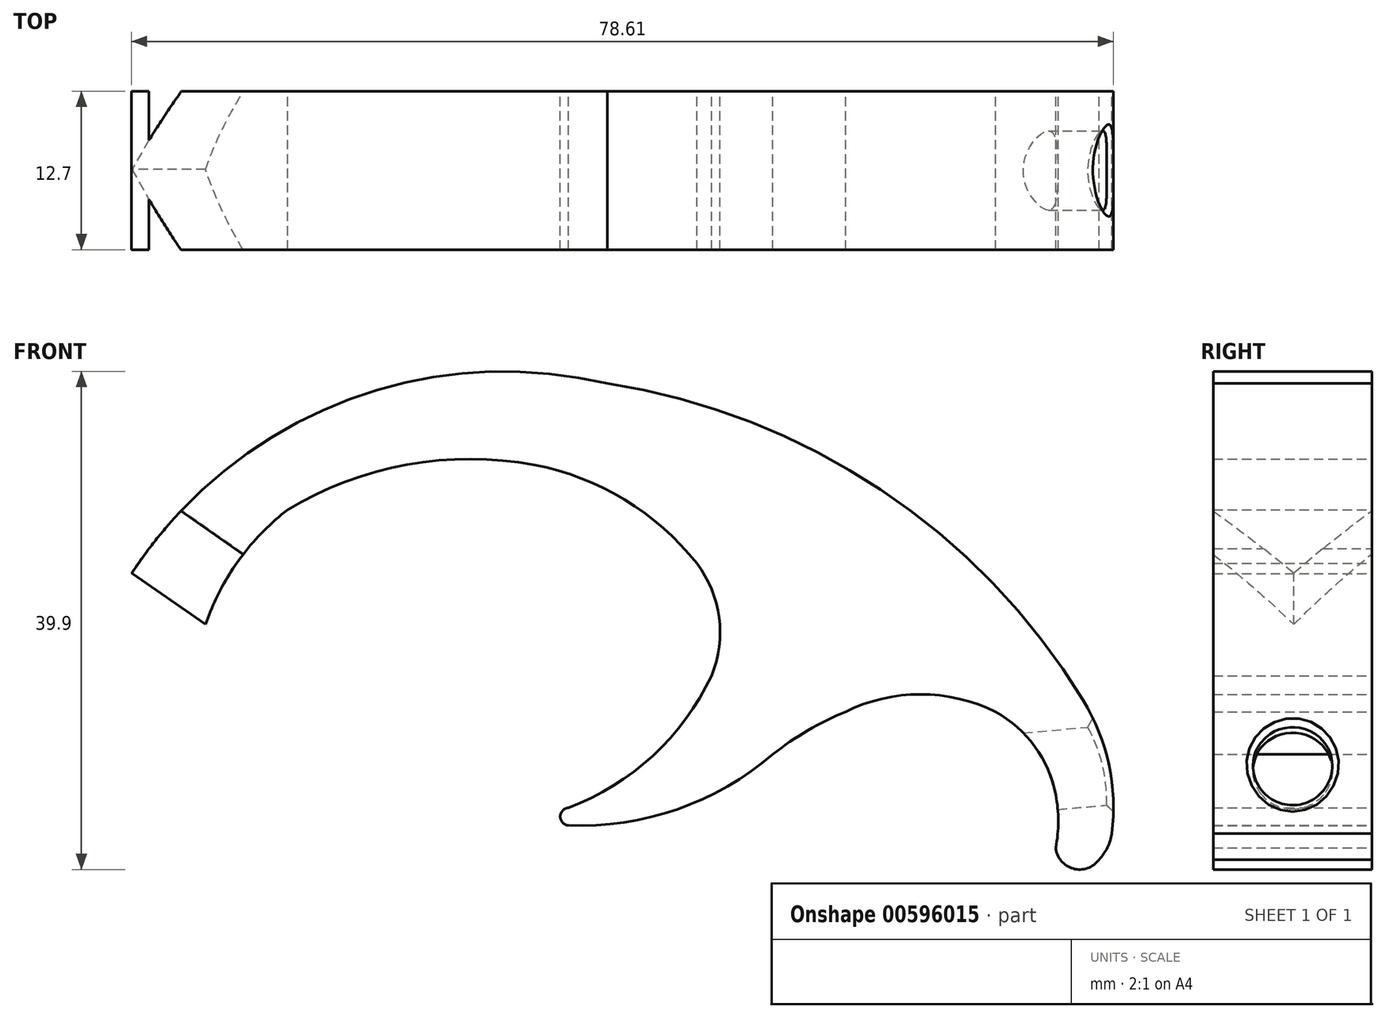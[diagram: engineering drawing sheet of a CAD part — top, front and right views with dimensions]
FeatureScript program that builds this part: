
annotation { "Feature Type Name" : "Feature", "Feature Type Description" : "" }
export const myFeature = defineFeature(function(context is Context, id is Id, definition is map)
    precondition{}
    {
        {
            var Q0;
            Q0=qCreatedBy(makeId("Front.planeOp"),FACE);
            var sketch = newSketch(context, id + "F0", { "sketchPlane" : qUnion([Q0])});
            skLineSegment(sketch, "E0", {"start": v(-79.66, 42.47) * mm, "end": v(-84.59, 51.35) * mm});
            skArc(sketch, "E1", {"start": v(-46.49, 66.6) * mm, "mid": v(-67.95, 65) * mm, "end": v(-84.59, 51.35) * mm});
            skArc(sketch, "E2", {"start": v(-8.39, 41.2) * mm, "mid": v(-24.63, 58.1) * mm, "end": v(-46.49, 66.6) * mm});
            skArc(sketch, "E3", {"start": v(-72.08, 56.48) * mm, "mid": v(-77.35, 50.27) * mm, "end": v(-79.66, 42.47) * mm});
            skArc(sketch, "E4", {"start": v(-52.32, 60.07) * mm, "mid": v(-62.53, 60.1) * mm, "end": v(-72.08, 56.48) * mm});
            skPoint(sketch, "E5.endSnap0", {"position": v(-24.63, 58.1) * mm});
            skArc(sketch, "E6", {"start": v(-10.6, 33.63) * mm, "mid": v(-12.26, 37.5) * mm, "end": v(-15.42, 40.3) * mm});
            skArc(sketch, "E7", {"start": v(-6.1, 30.53) * mm, "mid": v(-6.34, 36.05) * mm, "end": v(-8.39, 41.2) * mm});
            skArc(sketch, "E8", {"start": v(-7.14, 28.45) * mm, "mid": v(-6.46, 29.4) * mm, "end": v(-6.1, 30.53) * mm});
            skArc(sketch, "E9", {"start": v(-10.6, 29.4) * mm, "mid": v(-10.39, 31.52) * mm, "end": v(-10.6, 33.63) * mm});
            skPoint(sketch, "E9.startSnap0", {"position": v(-6.46, 29.4) * mm});
            skArc(sketch, "E10", {"start": v(-10.6, 29.4) * mm, "mid": v(-9.2, 27.73) * mm, "end": v(-7.14, 28.45) * mm});
            skArc(sketch, "E11", {"start": v(-39.33, 52.18) * mm, "mid": v(-45.12, 57.3) * mm, "end": v(-52.32, 60.07) * mm});
            skArc(sketch, "E12", {"start": v(-15.42, 40.3) * mm, "mid": v(-21.42, 41.7) * mm, "end": v(-27.42, 40.3) * mm});
            skArc(sketch, "E13", {"start": v(-27.42, 40.3) * mm, "mid": v(-30.45, 38.8) * mm, "end": v(-33.24, 36.89) * mm});
            skArc(sketch, "E14", {"start": v(-49.61, 31.2) * mm, "mid": v(-40.89, 32.48) * mm, "end": v(-33.24, 36.89) * mm});
            skArc(sketch, "E15", {"start": v(-49.61, 32.6) * mm, "mid": v(-50.27, 31.9) * mm, "end": v(-49.61, 31.2) * mm});
            skArc(sketch, "E16", {"start": v(-49.61, 32.6) * mm, "mid": v(-42.85, 36.77) * mm, "end": v(-38.15, 43.19) * mm});
            skArc(sketch, "E17", {"start": v(-38.15, 43.19) * mm, "mid": v(-37.55, 47.84) * mm, "end": v(-39.33, 52.18) * mm});
            skSolve(sketch);
        }
        {
            var Q0;
            Q0=qSketchRegion(id+"F0",true);
            extrude(context, id + "F1", {"entities" : qUnion([Q0]), "depth" : 12.7 * mm});
        }
        {
            var Q0;
            Q0=makeQuery(id+"F1.opExtrude","SWEPT_EDGE",EDGE,{"disambiguationData":[OSD([sQuery(id+"F0.wireOp",EDGE,"E0"),sQuery(id+"F0.wireOp",EDGE,"E1")])]});
            cPlane(context, id + "F2", {"entities" : qUnion([Q0]), "cplaneType" : CPlaneType.LINE_ANGLE, "offset" : 25.4 * mm, "angle" : 125 * degree, "width" : 152.4 * mm, "height" : 152.4 * mm});
        }
        {
            var Q0;
            Q0=qCreatedBy(id+"F2.planeOp",FACE);
            var sketch = newSketch(context, id + "F3", { "sketchPlane" : qUnion([Q0])});
            skLineSegment(sketch, "E18", {"start": v(0, 0) * mm, "end": v(-6.26, -6.38) * mm});
            skLineSegment(sketch, "E19", {"start": v(-6.26, -6.38) * mm, "end": v(-12.76, 0) * mm});
            skLineSegment(sketch, "E20", {"start": v(-12.76, 0) * mm, "end": v(-18.1, -16.76) * mm});
            skLineSegment(sketch, "E21", {"start": v(-18.1, -16.76) * mm, "end": v(3.4, -16.76) * mm});
            skLineSegment(sketch, "E22", {"start": v(3.4, -16.76) * mm, "end": v(0, 0) * mm});
            skSolve(sketch);
        }
        {
            var Q0;
            Q0=makeQuery(id+"F3.imprint","IMPRINT",FACE,{"disambiguationData":[TD([[makeQuery(id+"F3.imprint","IMPRINT",EDGE,{"derivedFrom":sQuery(id+"F3.wireOp",EDGE,"E18")}),1.0]])]});
            extrude(context, id + "F4", {"entities" : qUnion([Q0]), "operationType" : NewBodyOperationType.REMOVE, "depth" : 24.13 * mm});
        }
        {
            var Q0;
            Q0=makeQuery(id+"F1.opExtrude","SWEPT_EDGE",EDGE,{"disambiguationData":[OSD([sQuery(id+"F0.wireOp",EDGE,"E7"),sQuery(id+"F0.wireOp",EDGE,"E8")])]});
            cPlane(context, id + "F5", {"entities" : qUnion([Q0]), "cplaneType" : CPlaneType.LINE_ANGLE, "offset" : 25.4 * mm, "angle" : 85 * degree, "width" : 152.4 * mm, "height" : 152.4 * mm});
        }
        {
            var Q0;
            Q0=qCreatedBy(id+"F5.planeOp",FACE);
            var sketch = newSketch(context, id + "F6", { "sketchPlane" : qUnion([Q0])});
            skCircle(sketch, "E23", {"center": v(-6.35, 36.43) * mm, "radius": 3.18 * mm});
            skSolve(sketch);
        }
        {
            var Q0;
            Q0=makeQuery(id+"F6.imprint","IMPRINT",FACE,{"disambiguationData":[TD([[makeQuery(id+"F6.imprint","IMPRINT",EDGE,{"derivedFrom":sQuery(id+"F6.wireOp",EDGE,"E23")}),1.0]])]});
            extrude(context, id + "F7", {"entities" : qUnion([Q0]), "operationType" : NewBodyOperationType.REMOVE, "oppositeDirection" : true, "depth" : 17.27 * mm, "symmetric" : true});
        }
        {
            var Q0;
            Q0=makeQuery(id+"F7.boolean.opBoolean","INTERSECT",EDGE,{"derivedFrom":[makeQuery(id+"F1.opExtrude","SWEPT_FACE",FACE,{"disambiguationData":[OSD([sQuery(id+"F0.wireOp",EDGE,"E7")])]}),makeQuery(id+"F7.opExtrude","SWEPT_FACE",FACE,{"disambiguationData":[OSD([sQuery(id+"F6.wireOp",EDGE,"E23")])]})]});
            chamfer(context, id + "F8", {"entities" : qUnion([Q0]), "width" : 0.5 * mm, "tangentPropagation" : true});
        }
    });
